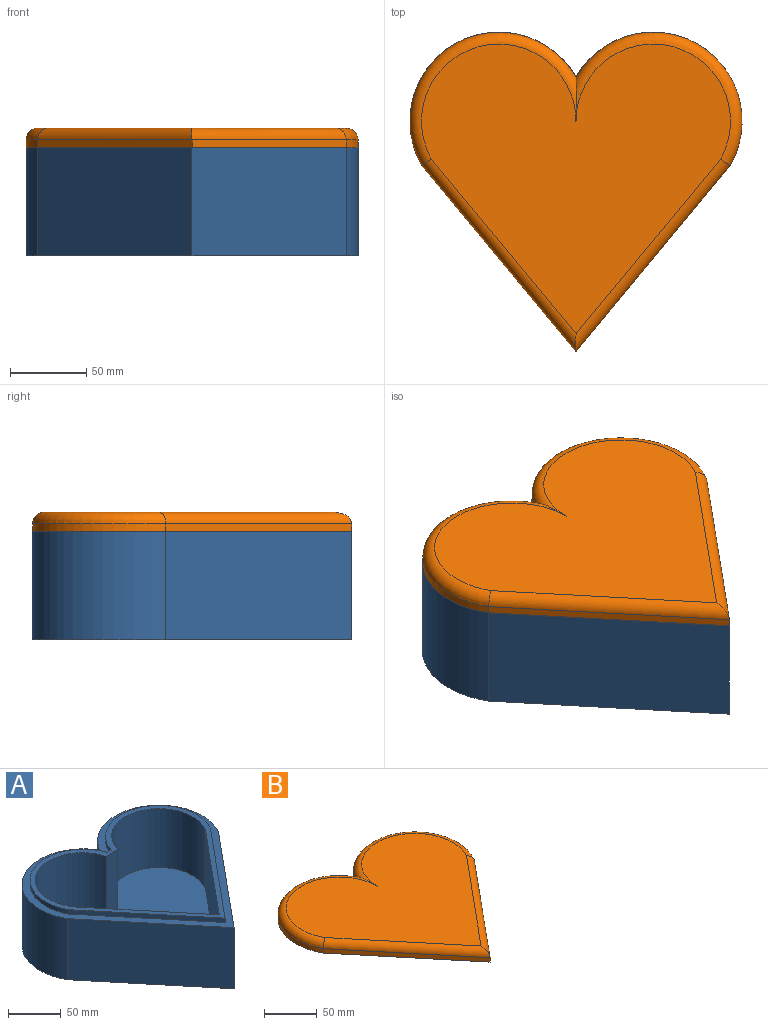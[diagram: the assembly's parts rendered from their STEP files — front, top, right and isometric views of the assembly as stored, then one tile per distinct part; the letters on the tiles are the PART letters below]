
ASSEMBLY  parts=2 mates=1
PART A: 18 faces, bbox 218.4x210.1x76.2 mm
  f0: plane 218.44x210.07mm, normal (0,0,1), area 5068mm2, adj f1,f2,f3,f4,f6,f7,f8,f9
  f1: plane 122.43x101.39mm, normal (-0.77,-0.64,0), area 11305.1mm2, adj f0,f2,f4,f5
  f2: plane 122.43x101.39mm, normal (0.77,-0.64,0), area 11305.1mm2, adj f0,f1,f3,f5
  f3: cylinder r=58.42mm len=109.22mm, axis (0,0,-1), area 13083.3mm2, adj f0,f2,f4,f5
  f4: cylinder r=58.42mm len=109.22mm, axis (0,0,-1), area 13083.3mm2, adj f0,f1,f3,f5
  f5: plane 218.44x210.07mm, normal (0,0,-1), area 29071.9mm2, adj f1,f2,f3,f4
  f6: cylinder r=50.8mm len=98.97mm, axis (0,0,-1), area 859.3mm2, adj f0,f7,f15,f16
  f7: plane 5.27x5.08mm, normal (0,1,0), area 26.8mm2, adj f0,f6,f8,f16
  f8: cylinder r=50.8mm len=98.97mm, axis (0,0,-1), area 859.3mm2, adj f0,f7,f9,f16
  f9: plane 114.83x95.1mm, normal (-0.77,-0.64,0), area 757.4mm2, adj f0,f8,f15,f16
  f10: plane 106.86x88.5mm, normal (0.77,0.64,0), area 9515.6mm2, adj f11,f14,f16,f17
  f11: cylinder r=44.97mm len=88.35mm, axis (0,0,-1), area 10715mm2, adj f10,f12,f16,f17
  f12: plane 68.58x15.96mm, normal (0,-1,0), area 1094.7mm2, adj f11,f13,f16,f17
  f13: cylinder r=44.97mm len=88.35mm, axis (0,0,-1), area 10715mm2, adj f12,f14,f16,f17
  f14: plane 106.86x88.5mm, normal (-0.77,0.64,0), area 9515.6mm2, adj f10,f13,f16,f17
  f15: plane 114.83x95.1mm, normal (0.77,-0.64,0), area 757.4mm2, adj f0,f6,f9,f16
  f16: plane 203.2x190.5mm, normal (0,0,1), area 3269.7mm2, adj f6,f7,f8,f9,f10,f11,f12,f13
  f17: plane 192.67x177.2mm, normal (0,0,1), area 20734.2mm2, adj f10,f11,f12,f13,f14
PART B: 16 faces, bbox 228.1x214.9x12.7 mm
  f0: plane 218.44x210.07mm, normal (0,0,-1), area 5068mm2, adj f1,f2,f3,f4,f10,f11,f12,f13
  f1: plane 122.43x101.39mm, normal (-0.77,-0.64,0), area 807.5mm2, adj f0,f2,f4,f6
  f2: plane 122.43x101.39mm, normal (0.77,-0.64,0), area 807.5mm2, adj f0,f1,f3,f8
  f3: cylinder r=58.42mm len=109.22mm, axis (0,0,-1), area 934.5mm2, adj f0,f2,f4,f9
  f4: cylinder r=58.42mm len=109.22mm, axis (0,0,-1), area 934.5mm2, adj f0,f1,f3,f7
  f5: plane 203.2x190.5mm, normal (0,0,1), area 23975.9mm2, adj f6,f7,f8,f9
  f6: cylinder r=7.62mm len=127.29mm, axis (-0.64,0.77,0), area 1859.8mm2, adj f1,f5,f7,f8
  f7: torus R=50.8mm, axis (0,0,1), area 2169.1mm2, adj f4,f5,f6,f9
  f8: cylinder r=7.62mm len=127.29mm, axis (-0.64,-0.77,0), area 1859.8mm2, adj f2,f5,f6,f9
  f9: torus R=50.8mm, axis (0,0,1), area 2169.1mm2, adj f3,f5,f7,f8
  f10: plane 114.83x95.1mm, normal (0.77,0.64,0), area 757.4mm2, adj f0,f11,f13,f14
  f11: plane 114.83x95.1mm, normal (-0.77,0.64,0), area 757.4mm2, adj f0,f10,f12,f14
  f12: cylinder r=50.8mm len=98.97mm, axis (0,0,-1), area 859.3mm2, adj f0,f11,f14,f15
  f13: cylinder r=50.8mm len=98.97mm, axis (0,0,-1), area 859.3mm2, adj f0,f10,f14,f15
  f14: plane 203.2x190.5mm, normal (0,0,-1), area 24004mm2, adj f10,f11,f12,f13,f15
  f15: plane 5.27x5.08mm, normal (0,-1,0), area 26.8mm2, adj f0,f12,f13,f14
PLACE A at identity fixed
PLACE B t=(0,-0.33,0)mm
MATE slider B.f14 <-> A.f17  axis (0,0,1) through (0,43.71,68.58)mm
